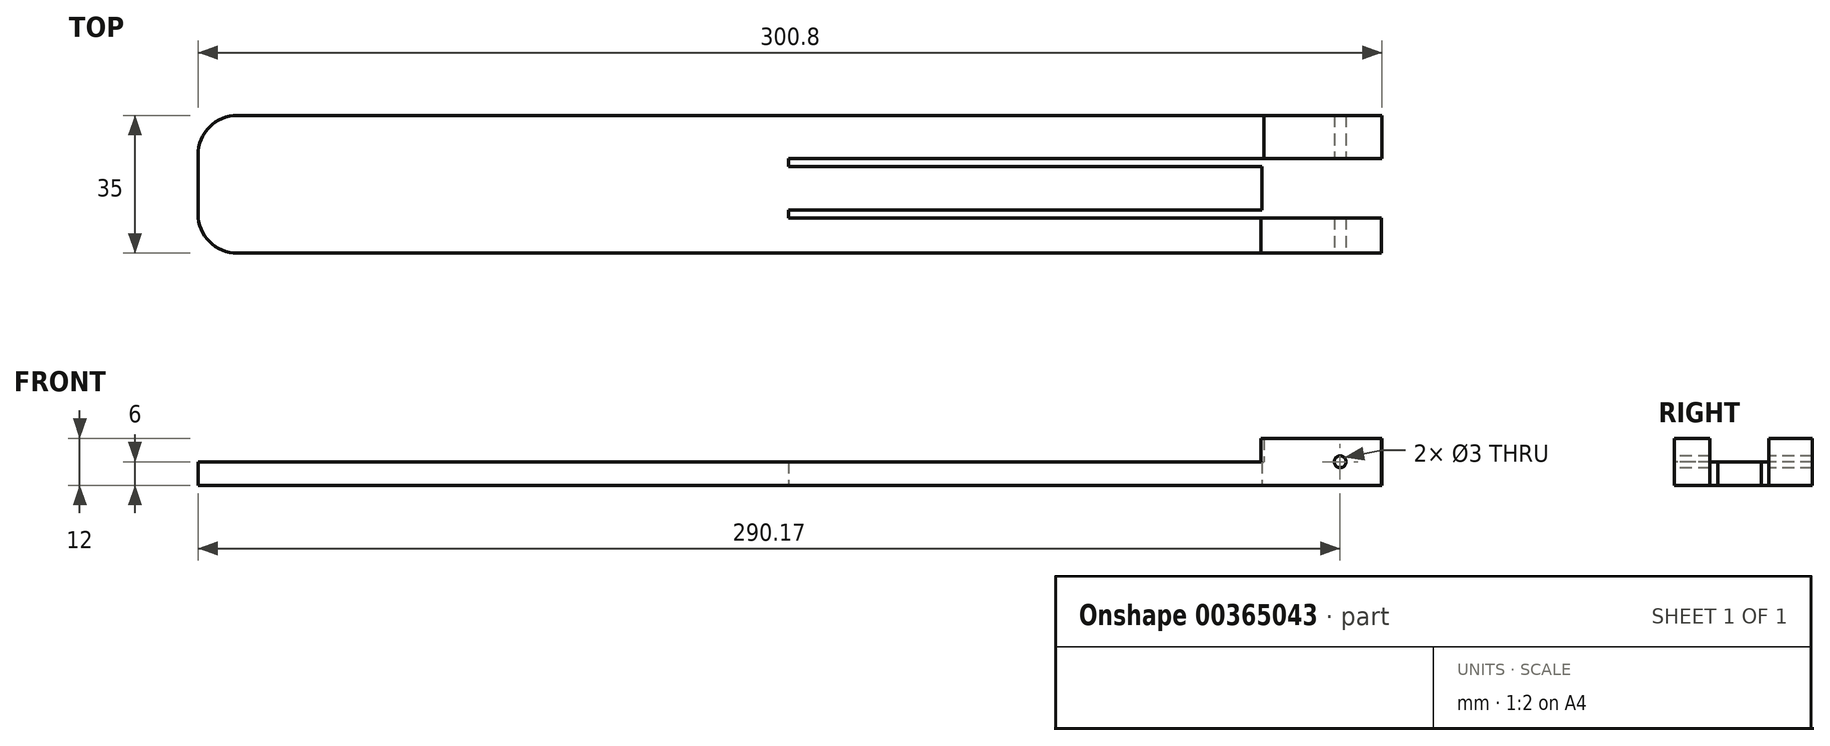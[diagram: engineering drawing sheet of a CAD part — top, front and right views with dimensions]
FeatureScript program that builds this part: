
annotation { "Feature Type Name" : "Feature", "Feature Type Description" : "" }
export const myFeature = defineFeature(function(context is Context, id is Id, definition is map)
    precondition{}
    {
        {
            var Q0;
            Q0=qCreatedBy(makeId("Top.planeOp"),FACE);
            var sketch = newSketch(context, id + "F0", { "sketchPlane" : qUnion([Q0])});
            skLineSegment(sketch, "E0.bottom", {"start": v(-150, 17.5) * mm, "end": v(120, 17.5) * mm});
            skLineSegment(sketch, "E0.top", {"start": v(-150, -17.5) * mm, "end": v(120, -17.5) * mm});
            skLineSegment(sketch, "E0.left", {"start": v(-150, 17.5) * mm, "end": v(-150, -17.5) * mm});
            skPoint(sketch, "E0.middle", {"position": v(0, 0) * mm});
            skLineSegment(sketch, "E1", {"start": v(0, 6.5) * mm, "end": v(120, 6.5) * mm});
            skLineSegment(sketch, "E2", {"start": v(0, 4.5) * mm, "end": v(150, 4.5) * mm});
            skLineSegment(sketch, "E3", {"start": v(0, -8.5) * mm, "end": v(120, -8.5) * mm});
            skLineSegment(sketch, "E4", {"start": v(0, -6.5) * mm, "end": v(150, -6.5) * mm});
            skLineSegment(sketch, "E5", {"start": v(0, -6.5) * mm, "end": v(0, -8.5) * mm});
            skLineSegment(sketch, "E6", {"start": v(0, 6.5) * mm, "end": v(0, 4.5) * mm});
            skLineSegment(sketch, "E7.trimOffspring", {"start": v(150, 4.5) * mm, "end": v(150, -6.5) * mm});
            skLineSegment(sketch, "E8", {"start": v(120, 17.5) * mm, "end": v(120, 6.5) * mm});
            skPoint(sketch, "E0.right.start.orphan", {"position": v(150, 17.5) * mm});
            skPoint(sketch, "E9.trimOffspring.start.orphan", {"position": v(150, -8.5) * mm});
            skPoint(sketch, "E10.orphan", {"position": v(150, -17.5) * mm});
            skLineSegment(sketch, "E11.trimOffspring", {"start": v(120, -8.5) * mm, "end": v(120, -17.5) * mm});
            skSolve(sketch);
        }
        {
            var Q0;
            Q0=makeQuery(id+"F0.imprint","IMPRINT",FACE,{"disambiguationData":[TD([[makeQuery(id+"F0.imprint","IMPRINT",EDGE,{"derivedFrom":sQuery(id+"F0.wireOp",EDGE,"E0.bottom")}),-1.0]])]});
            extrude(context, id + "F1", {"entities" : qUnion([Q0]), "depth" : 6 * mm});
        }
        {
            var Q0;
            Q0=makeQuery(id+"F1.opExtrude","SWEPT_EDGE",EDGE,{"disambiguationData":[OSD([sQuery(id+"F0.wireOp",EDGE,"E0.top"),sQuery(id+"F0.wireOp",EDGE,"E0.left")])]});
            var Q1;
            Q1=makeQuery(id+"F1.opExtrude","SWEPT_EDGE",EDGE,{"disambiguationData":[OSD([sQuery(id+"F0.wireOp",EDGE,"E0.bottom"),sQuery(id+"F0.wireOp",EDGE,"E0.left")])]});
            fillet(context, id + "F2", {"entities" : qUnion([Q0, Q1]), "radius" : 10 * mm, "tangentPropagation" : true, "allowEdgeOverflow" : false});
        }
        {
            var Q0;
            Q0=makeQuery(id+"F1.opExtrude","SWEPT_FACE",FACE,{"disambiguationData":[OSD([sQuery(id+"F0.wireOp",EDGE,"E11.trimOffspring")])]});
            extrude(context, id + "F3", {"entities" : qUnion([Q0]), "operationType" : NewBodyOperationType.ADD, "depth" : 30.67 * mm});
        }
        {
            var Q0;
            Q0=makeQuery(id+"F1.opExtrude","SWEPT_FACE",FACE,{"disambiguationData":[OSD([sQuery(id+"F0.wireOp",EDGE,"E8")])]});
            extrude(context, id + "F4", {"entities" : qUnion([Q0]), "operationType" : NewBodyOperationType.ADD, "depth" : 30.8 * mm});
        }
        {
            var Q0;
            Q0=makeQuery(id+"F1.opExtrude","SWEPT_FACE",FACE,{"disambiguationData":[OSD([sQuery(id+"F0.wireOp",EDGE,"E7.trimOffspring")])]});
            extrude(context, id + "F5", {"entities" : qUnion([Q0]), "operationType" : NewBodyOperationType.REMOVE, "oppositeDirection" : true, "depth" : 29.7 * mm});
        }
        {
            var Q0;
            {var subQ0=sQuery(id+"F0.wireOp",EDGE,"E8");var subQ1=sQuery(id+"F0.wireOp",EDGE,"E11.trimOffspring");Q0=makeQuery(id+"F4.boolean.opBoolean","MERGE",FACE,{"derivedFrom":[makeQuery(id+"F3.boolean.opBoolean","MERGE",FACE,{"derivedFrom":[makeQuery(id+"F1.opExtrude","CAP_FACE",FACE,{"disambiguationData":[OSD([sQuery(id+"F0.wireOp",EDGE,"E0.bottom"),sQuery(id+"F0.wireOp",EDGE,"E0.top"),sQuery(id+"F0.wireOp",EDGE,"E0.left"),sQuery(id+"F0.wireOp",EDGE,"E1"),sQuery(id+"F0.wireOp",EDGE,"E2"),sQuery(id+"F0.wireOp",EDGE,"E3"),sQuery(id+"F0.wireOp",EDGE,"E4"),sQuery(id+"F0.wireOp",EDGE,"E5"),sQuery(id+"F0.wireOp",EDGE,"E6"),sQuery(id+"F0.wireOp",EDGE,"E7.trimOffspring"),subQ0,subQ1])],"isStart":false}),makeQuery(id+"F3.opExtrude","SWEPT_FACE",FACE,{"disambiguationData":[OSD([subQ1]),TDD([makeQuery(id+"F1.opExtrude","CAP_EDGE",EDGE,{"disambiguationData":[OSD([subQ1])],"isStart":false})])]})]}),makeQuery(id+"F4.opExtrude","SWEPT_FACE",FACE,{"disambiguationData":[OSD([subQ0]),TDD([makeQuery(id+"F1.opExtrude","CAP_EDGE",EDGE,{"disambiguationData":[OSD([subQ0])],"isStart":false})])]})]});}
            var sketch = newSketch(context, id + "F6", { "sketchPlane" : qUnion([Q0])});
            skLineSegment(sketch, "E12.bottom", {"start": v(120.8, 17.5) * mm, "end": v(150.8, 17.5) * mm});
            skLineSegment(sketch, "E12.top", {"start": v(120.8, 6.5) * mm, "end": v(150.8, 6.5) * mm});
            skLineSegment(sketch, "E12.left", {"start": v(120.8, 17.5) * mm, "end": v(120.8, 6.5) * mm});
            skLineSegment(sketch, "E12.right", {"start": v(150.8, 17.5) * mm, "end": v(150.8, 6.5) * mm});
            skLineSegment(sketch, "E13.bottom", {"start": v(120, -8.5) * mm, "end": v(150.67, -8.5) * mm});
            skLineSegment(sketch, "E13.top", {"start": v(120, -17.5) * mm, "end": v(150.67, -17.5) * mm});
            skLineSegment(sketch, "E13.left", {"start": v(120, -8.5) * mm, "end": v(120, -17.5) * mm});
            skLineSegment(sketch, "E13.right", {"start": v(150.67, -8.5) * mm, "end": v(150.67, -17.5) * mm});
            skSolve(sketch);
        }
        {
            var Q0;
            Q0=makeQuery(id+"F6.imprint","IMPRINT",FACE,{"disambiguationData":[TD([[makeQuery(id+"F6.imprint","IMPRINT",EDGE,{"derivedFrom":sQuery(id+"F6.wireOp",EDGE,"E12.bottom")}),-1.0]])]});
            var Q1;
            Q1=makeQuery(id+"F6.imprint","IMPRINT",FACE,{"disambiguationData":[TD([[makeQuery(id+"F6.imprint","IMPRINT",EDGE,{"derivedFrom":sQuery(id+"F6.wireOp",EDGE,"E13.bottom")}),-1.0]])]});
            extrude(context, id + "F7", {"entities" : qUnion([Q0, Q1]), "operationType" : NewBodyOperationType.ADD, "depth" : 6 * mm});
        }
        {
            var Q0;
            {var subQ0=sQuery(id+"F0.wireOp",EDGE,"E0.top");Q0=makeQuery(id+"F7.boolean.opBoolean","MERGE",FACE,{"derivedFrom":[makeQuery(id+"F3.boolean.opBoolean","MERGE",FACE,{"derivedFrom":[makeQuery(id+"F1.opExtrude","SWEPT_FACE",FACE,{"disambiguationData":[OSD([subQ0])]}),makeQuery(id+"F3.opExtrude","SWEPT_FACE",FACE,{"disambiguationData":[OSD([subQ0,sQuery(id+"F0.wireOp",EDGE,"E11.trimOffspring")])]})]}),makeQuery(id+"F7.opExtrude","SWEPT_FACE",FACE,{"disambiguationData":[OSD([sQuery(id+"F6.wireOp",EDGE,"E13.top")])]})]});}
            var sketch = newSketch(context, id + "F8", { "sketchPlane" : qUnion([Q0])});
            skCircle(sketch, "E14", {"center": v(140.17, 6) * mm, "radius": 1.5 * mm});
            skPoint(sketch, "E14.centerSnap0", {"position": v(150.67, 6) * mm});
            skSolve(sketch);
        }
        {
            var Q0;
            Q0=makeQuery(id+"F8.imprint","IMPRINT",FACE,{"disambiguationData":[TD([[makeQuery(id+"F8.imprint","IMPRINT",EDGE,{"derivedFrom":sQuery(id+"F8.wireOp",EDGE,"E14")}),1.0]])]});
            extrude(context, id + "F9", {"entities" : qUnion([Q0]), "operationType" : NewBodyOperationType.REMOVE, "oppositeDirection" : true, "depth" : 37.3 * mm});
        }
    });
